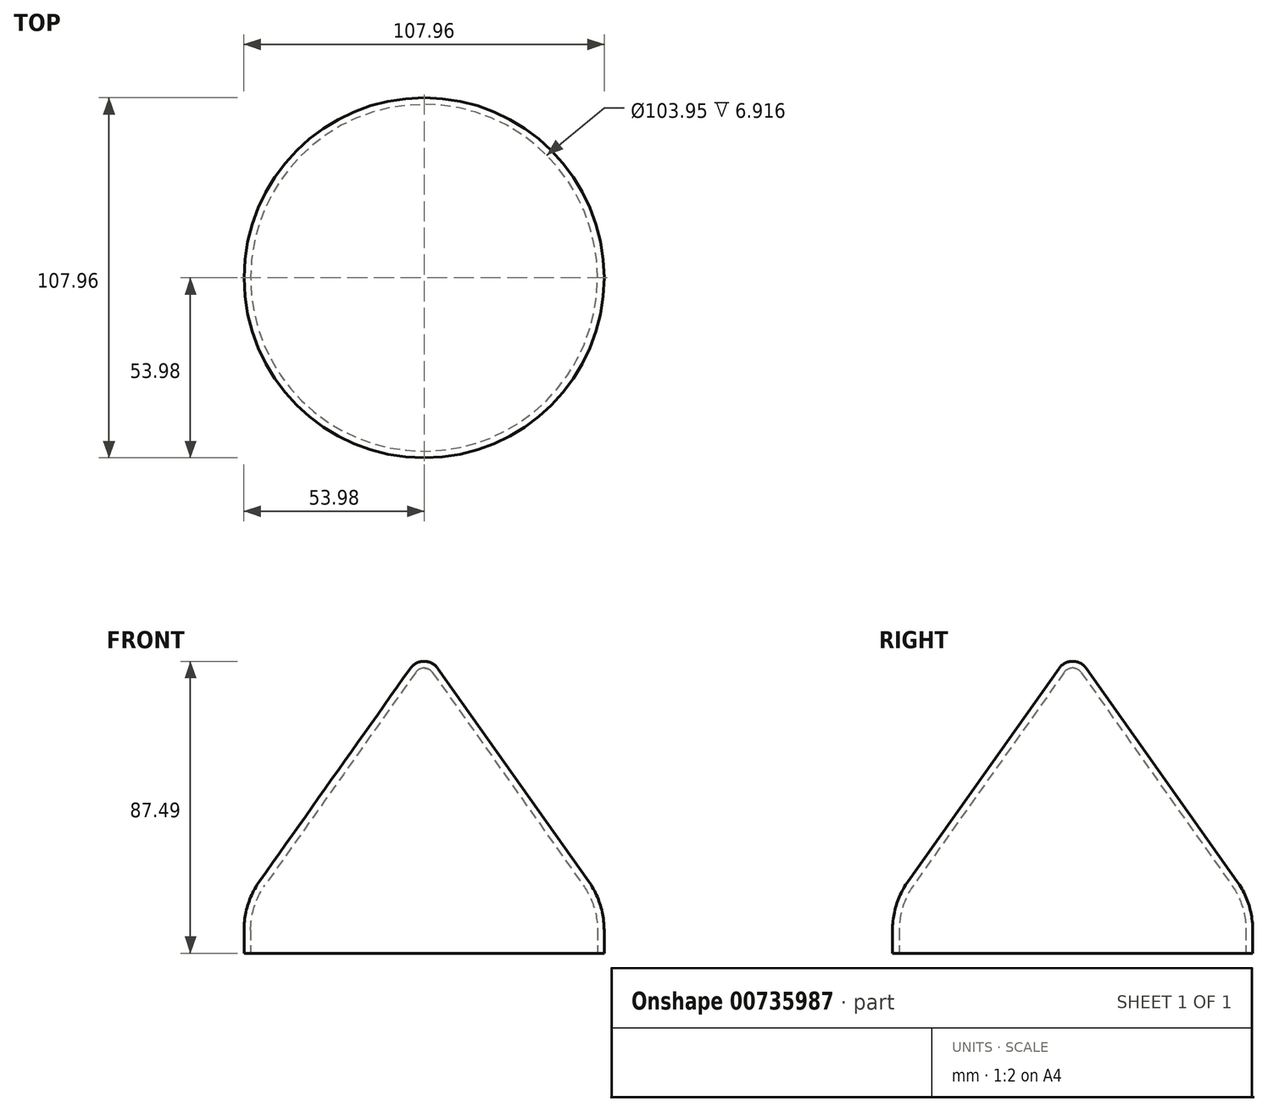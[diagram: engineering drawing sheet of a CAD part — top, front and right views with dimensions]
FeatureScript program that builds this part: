
annotation { "Feature Type Name" : "Feature", "Feature Type Description" : "" }
export const myFeature = defineFeature(function(context is Context, id is Id, definition is map)
    precondition{}
    {
        {
            var Q0;
            Q0=qCreatedBy(makeId("Front.planeOp"),FACE);
            var sketch = newSketch(context, id + "F0", { "sketchPlane" : qUnion([Q0])});
            skLineSegment(sketch, "E0", {"start": v(0, 76.2) * mm, "end": v(53.98, 0) * mm});
            skLineSegment(sketch, "E1", {"start": v(53.98, 0) * mm, "end": v(0, 0) * mm});
            skLineSegment(sketch, "E2", {"start": v(0, 0) * mm, "end": v(0, 76.2) * mm});
            skArc(sketch, "E3", {"start": v(0, 72.5) * mm, "mid": v(2.33, 71.92) * mm, "end": v(4.15, 70.35) * mm});
            skLineSegment(sketch, "E4.bottom", {"start": v(0, 0) * mm, "end": v(53.98, 0) * mm, "construction": true});
            skLineSegment(sketch, "E4.top", {"start": v(0, -15) * mm, "end": v(53.98, -15) * mm});
            skLineSegment(sketch, "E4.left", {"start": v(0, 0) * mm, "end": v(0, -15) * mm});
            skLineSegment(sketch, "E4.right", {"start": v(53.98, 0) * mm, "end": v(53.98, -15) * mm});
            skSolve(sketch);
        }
        {
            var Q0;
            {var subQ0=sQuery(id+"F0.wireOp",EDGE,"E1");Q0=makeQuery(id+"F0.imprint","IMPRINT",FACE,{"disambiguationData":[TD([[makeQuery(id+"F0.imprint","IMPRINT",EDGE,{"derivedFrom":subQ0}),-1.0]])]});}
            var Q1;
            Q1=makeQuery(id+"F0.imprint","IMPRINT",FACE,{"disambiguationData":[TD([[makeQuery(id+"F0.imprint","IMPRINT",EDGE,{"derivedFrom":sQuery(id+"F0.wireOp",EDGE,"E1")}),1.0]])]});
            var Q2;
            Q2=sQuery(id+"F0.wireOp",EDGE,"E2");
            revolve(context, id + "F1", {"surfaceOperationType" : NewSurfaceOperationType.NEW, "entities" : qUnion([Q0, Q1]), "axis" : qUnion([Q2]), "revolveType" : RevolveType.FULL});
        }
        {
            var Q0;
            Q0=makeQuery(id+"F1.opRevolve","SWEPT_EDGE",EDGE,{"disambiguationData":[OSD([sQuery(id+"F0.wireOp",EDGE,"E0"),sQuery(id+"F0.wireOp",EDGE,"E1"),sQuery(id+"F0.wireOp",EDGE,"E4.right")])]});
            fillet(context, id + "F2", {"entities" : qUnion([Q0]), "radius" : 25.4 * mm, "tangentPropagation" : true, "allowEdgeOverflow" : false});
        }
        {
            var Q0;
            Q0=makeQuery(id+"F1.opRevolve","SWEPT_FACE",FACE,{"disambiguationData":[OSD([sQuery(id+"F0.wireOp",EDGE,"E4.top")])]});
            shell(context, id + "F3", {"entities" : qUnion([Q0]), "thickness" : 2 * mm});
        }
    });
